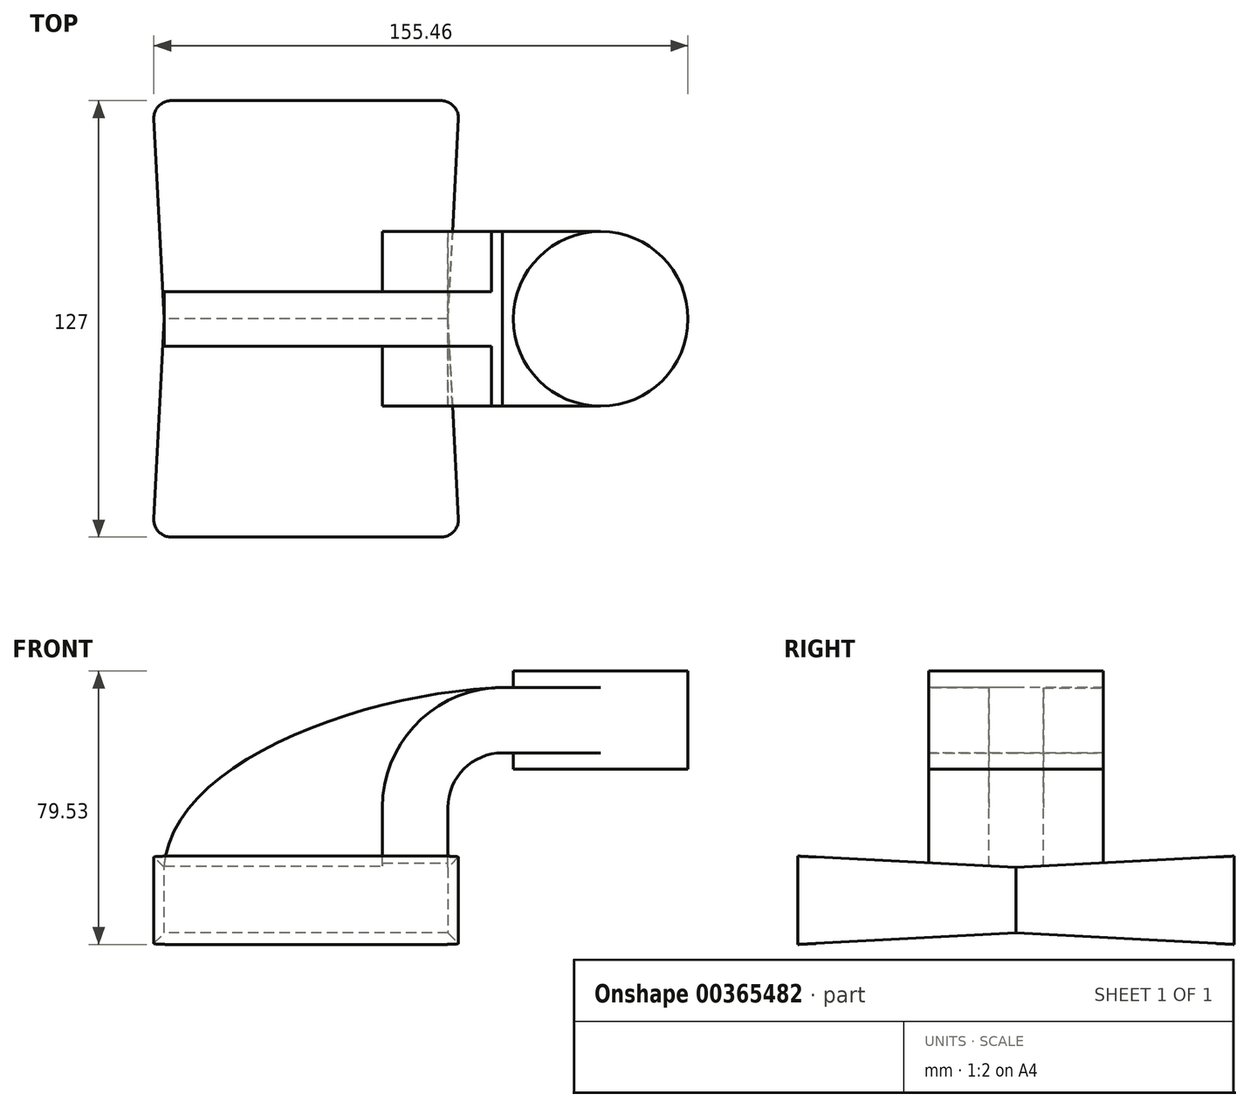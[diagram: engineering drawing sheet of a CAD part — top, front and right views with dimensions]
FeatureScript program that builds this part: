
annotation { "Feature Type Name" : "Feature", "Feature Type Description" : "" }
export const myFeature = defineFeature(function(context is Context, id is Id, definition is map)
    precondition{}
    {
        {
            var Q0;
            Q0=qCreatedBy(makeId("Front.planeOp"),FACE);
            var sketch = newSketch(context, id + "F0", { "sketchPlane" : qUnion([Q0])});
            skLineSegment(sketch, "E0.rect.bottom", {"start": v(-41.28, 9.52) * mm, "end": v(41.28, 9.52) * mm});
            skLineSegment(sketch, "E0.rect.top", {"start": v(-41.28, -9.52) * mm, "end": v(41.28, -9.52) * mm});
            skLineSegment(sketch, "E0.rect.left", {"start": v(-41.28, 9.52) * mm, "end": v(-41.28, -9.52) * mm});
            skLineSegment(sketch, "E0.rect.right", {"start": v(41.28, 9.52) * mm, "end": v(41.28, -9.52) * mm});
            skPoint(sketch, "E0.rect.middle", {"position": v(0, 0) * mm});
            skLineSegment(sketch, "E1", {"start": v(41.28, 9.52) * mm, "end": v(41.28, 27) * mm});
            skArc(sketch, "E2", {"start": v(41.28, 27) * mm, "mid": v(45.92, 38.23) * mm, "end": v(57.15, 42.88) * mm});
            skLineSegment(sketch, "E3", {"start": v(57.15, 42.88) * mm, "end": v(85.72, 42.88) * mm});
            skLineSegment(sketch, "E4.rect.bottom", {"start": v(60.32, 38.1) * mm, "end": v(111.12, 38.1) * mm});
            skLineSegment(sketch, "E4.rect.top", {"start": v(60.32, 66.68) * mm, "end": v(111.12, 66.68) * mm});
            skLineSegment(sketch, "E4.rect.left", {"start": v(60.32, 38.1) * mm, "end": v(60.32, 66.68) * mm});
            skLineSegment(sketch, "E4.rect.right", {"start": v(111.13, 38.1) * mm, "end": v(111.12, 66.68) * mm});
            skPoint(sketch, "E4.rect.middle", {"position": v(85.72, 52.39) * mm});
            skLineSegment(sketch, "E5.0", {"start": v(57.15, 61.93) * mm, "end": v(85.72, 61.93) * mm});
            skArc(sketch, "E5.1", {"start": v(22.23, 27) * mm, "mid": v(32.45, 51.7) * mm, "end": v(57.15, 61.93) * mm});
            skLineSegment(sketch, "E5.2", {"start": v(22.23, 9.52) * mm, "end": v(22.23, 27) * mm});
            skLineSegment(sketch, "E6", {"start": v(85.72, 38.1) * mm, "end": v(85.72, 66.68) * mm});
            skFitSpline(sketch, "E7", {"points": [v(-41.28, 9.53) * mm, v(57.15, 61.93) * mm], "startDerivative": vector(5.2, 92.34) * mm, "endDerivative": vector(120.92, 4.22) * mm});
            skSolve(sketch);
        }
        {
            var Q0;
            Q0=makeQuery(id+"F0.imprint","IMPRINT",FACE,{"disambiguationData":[TD([[makeQuery(id+"F0.imprint","IMPRINT",EDGE,{"derivedFrom":sQuery(id+"F0.wireOp",EDGE,"E0.rect.top")}),1.0]])]});
            extrude(context, id + "F1", {"entities" : qUnion([Q0]), "endBound" : BoundingType.SYMMETRIC, "depth" : 127 * mm, "hasDraft" : true, "draftAngle" : 3 * degree});
        }
        {
            var Q0;
            {var subQ9=sQuery(id+"F0.wireOp",EDGE,"E1");Q0=makeQuery(id+"F0.imprint","IMPRINT",FACE,{"disambiguationData":[TD([[makeQuery(id+"F0.imprint","IMPRINT",EDGE,{"derivedFrom":subQ9}),1.0]])]});}
            var Q1;
            {var subQ0=sQuery(id+"F0.wireOp",EDGE,"E6");var subQ1=sQuery(id+"F0.wireOp",EDGE,"E3");var subQ2=makeQuery(id+"F0.imprint","INTERSECT",VERTEX,{"derivedFrom":[subQ1,subQ0]});Q1=makeQuery(id+"F0.imprint","IMPRINT",FACE,{"disambiguationData":[TD([[makeQuery(id+"F0.imprint","IMPRINT",EDGE,{"disambiguationData":[TD([[subQ2,1.0]])],"derivedFrom":subQ1}),1.0]])]});}
            var Q2;
            Q2=makeQuery(id+"F1.*.split.splitOp","SPLIT",BODY,{"derivedFrom":makeQuery(id+"F1.opExtrude","SWEPT_BODY",BODY,{"disambiguationData":[OSD([sQuery(id+"F0.wireOp",EDGE,"E0.rect.bottom"),sQuery(id+"F0.wireOp",EDGE,"E0.rect.top"),sQuery(id+"F0.wireOp",EDGE,"E0.rect.left"),sQuery(id+"F0.wireOp",EDGE,"E0.rect.right")])]})});
            extrude(context, id + "F2", {"entities" : qUnion([Q0, Q1]), "operationType" : NewBodyOperationType.ADD, "endBound" : BoundingType.SYMMETRIC, "endBoundEntityBody" : qUnion([Q2]), "depth" : 50.8 * mm});
        }
        {
            var Q0;
            {var subQ3=sQuery(id+"F0.wireOp",EDGE,"E5.2");Q0=makeQuery(id+"F0.imprint","IMPRINT",FACE,{"disambiguationData":[TD([[makeQuery(id+"F0.imprint","IMPRINT",EDGE,{"derivedFrom":subQ3}),1.0]])]});}
            extrude(context, id + "F3", {"entities" : qUnion([Q0]), "operationType" : NewBodyOperationType.ADD, "endBound" : BoundingType.SYMMETRIC, "depth" : 15.88 * mm});
        }
        {
            var Q0;
            {var subQ5=sQuery(id+"F0.wireOp",EDGE,"E4.rect.right");Q0=makeQuery(id+"F0.imprint","IMPRINT",FACE,{"disambiguationData":[TD([[makeQuery(id+"F0.imprint","IMPRINT",EDGE,{"derivedFrom":subQ5}),1.0]])]});}
            var Q1;
            Q1=sQuery(id+"F0.wireOp",EDGE,"E6");
            revolve(context, id + "F4", {"operationType" : NewBodyOperationType.ADD, "entities" : qUnion([Q0]), "axis" : qUnion([Q1]), "revolveType" : RevolveType.FULL});
        }
        {
            var Q0;
            Q0=makeQuery(id+"F1.opExtrude","CAP_EDGE",EDGE,{"disambiguationData":[OSD([sQuery(id+"F0.wireOp",EDGE,"E0.rect.right")])],"isStart":false});
            var Q1;
            Q1=makeQuery(id+"F1.opExtrude","CAP_EDGE",EDGE,{"disambiguationData":[OSD([sQuery(id+"F0.wireOp",EDGE,"E0.rect.left")])],"isStart":false});
            var Q2;
            Q2=makeQuery(id+"F1.opExtrude","CAP_EDGE",EDGE,{"disambiguationData":[OSD([sQuery(id+"F0.wireOp",EDGE,"E0.rect.right")])],"isStart":true});
            var Q3;
            Q3=makeQuery(id+"F1.opExtrude","CAP_EDGE",EDGE,{"disambiguationData":[OSD([sQuery(id+"F0.wireOp",EDGE,"E0.rect.left")])],"isStart":true});
            fillet(context, id + "F5", {"entities" : qUnion([Q0, Q1, Q2, Q3]), "radius" : 5.08 * mm, "tangentPropagation" : true, "allowEdgeOverflow" : false});
        }
    });
